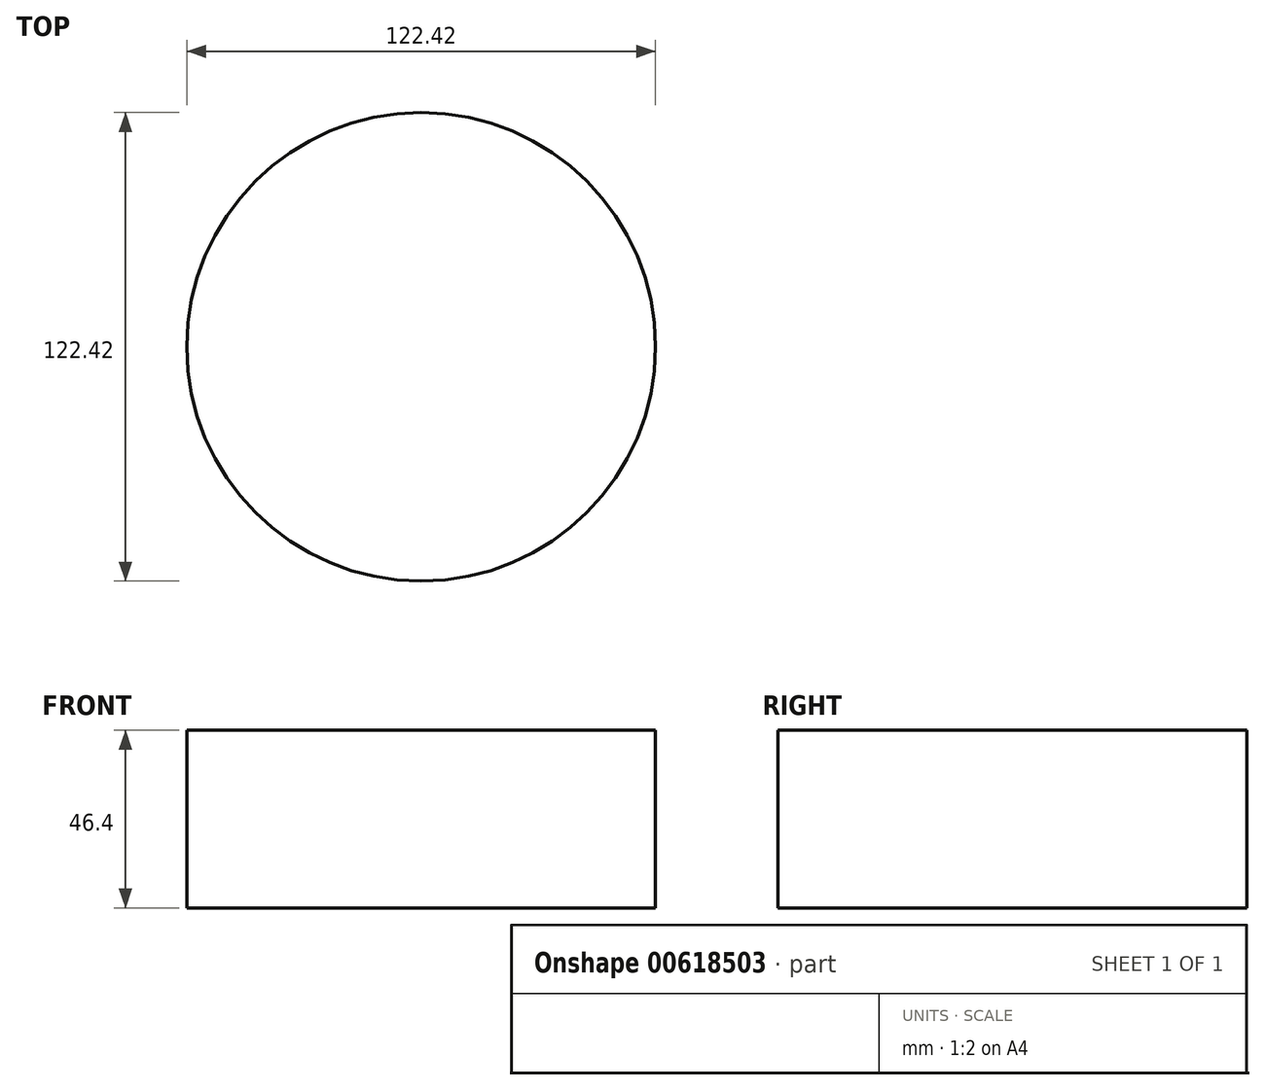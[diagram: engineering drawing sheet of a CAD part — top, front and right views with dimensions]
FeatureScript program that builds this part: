
annotation { "Feature Type Name" : "Feature", "Feature Type Description" : "" }
export const myFeature = defineFeature(function(context is Context, id is Id, definition is map)
    precondition{}
    {
        {
            var Q0;
            Q0=qCreatedBy(makeId("Top.planeOp"),FACE);
            var sketch = newSketch(context, id + "F0", { "sketchPlane" : qUnion([Q0])});
            skCircle(sketch, "E0", {"center": v(0, 0) * mm, "radius": 61.2 * mm});
            skSolve(sketch);
        }
        {
            var Q0;
            Q0=makeQuery(id+"F0.imprint","IMPRINT",FACE,{"disambiguationData":[TD([[makeQuery(id+"F0.imprint","IMPRINT",EDGE,{"derivedFrom":sQuery(id+"F0.wireOp",EDGE,"E0")}),1.0]])]});
            extrude(context, id + "F1", {"entities" : qUnion([Q0]), "depth" : 46.4 * mm, "offsetDistance" : 25 * mm});
        }
    });
